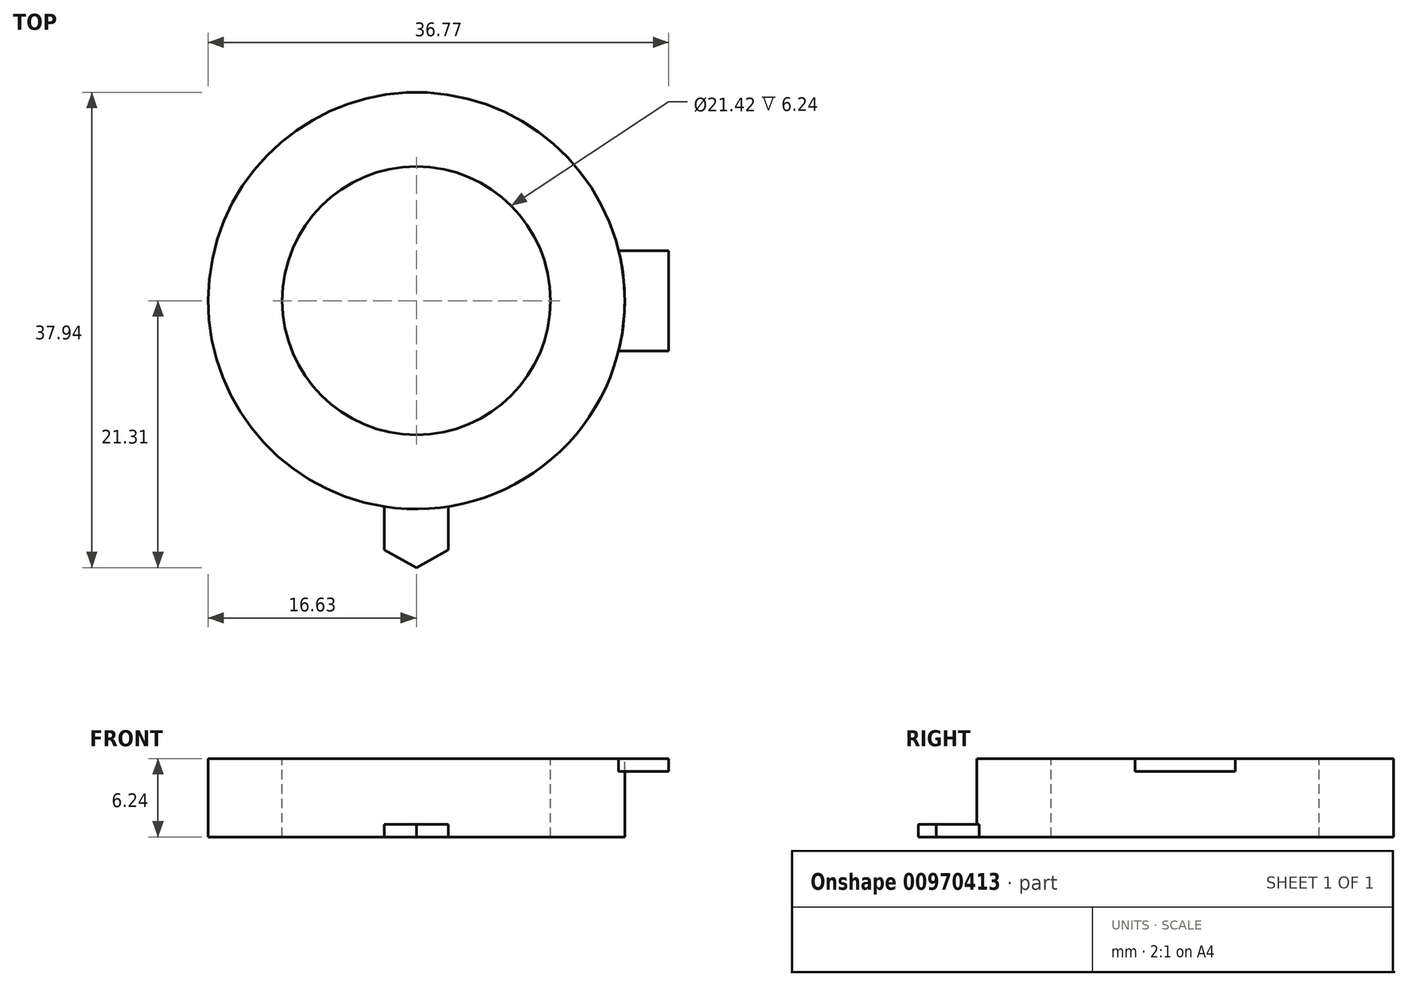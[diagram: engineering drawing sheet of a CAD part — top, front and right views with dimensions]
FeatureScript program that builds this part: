
annotation { "Feature Type Name" : "Feature", "Feature Type Description" : "" }
export const myFeature = defineFeature(function(context is Context, id is Id, definition is map)
    precondition{}
    {
        {
            var Q0;
            Q0=qCreatedBy(makeId("Top.planeOp"),FACE);
            var sketch = newSketch(context, id + "F0", { "sketchPlane" : qUnion([Q0])});
            skCircle(sketch, "E0", {"center": v(0, 0) * mm, "radius": 16.63 * mm});
            skLineSegment(sketch, "E1", {"start": v(0, 0) * mm, "end": v(0, -16.63) * mm, "construction": true});
            skLineSegment(sketch, "E2", {"start": v(-2.56, -16.43) * mm, "end": v(-2.56, -19.9) * mm});
            skLineSegment(sketch, "E3", {"start": v(-2.56, -19.9) * mm, "end": v(0, -21.31) * mm});
            skLineSegment(sketch, "E4", {"start": v(0, -21.3) * mm, "end": v(2.56, -19.9) * mm});
            skLineSegment(sketch, "E5", {"start": v(0, -21.31) * mm, "end": v(0, 16.63) * mm, "construction": true});
            skLineSegment(sketch, "E6", {"start": v(2.56, -19.9) * mm, "end": v(2.56, -16.43) * mm});
            skLineSegment(sketch, "E7", {"start": v(-2.56, -18.16) * mm, "end": v(0, -18.16) * mm, "construction": true});
            skLineSegment(sketch, "E8", {"start": v(0, -18.16) * mm, "end": v(2.56, -18.16) * mm, "construction": true});
            skSolve(sketch);
        }
        {
            var Q0;
            Q0=makeQuery(id+"F0.imprint","IMPRINT",FACE,{"disambiguationData":[TD([[makeQuery(id+"F0.imprint","IMPRINT",EDGE,{"derivedFrom":sQuery(id+"F0.wireOp",EDGE,"E0")}),1.0]])]});
            extrude(context, id + "F1", {"entities" : qUnion([Q0]), "depth" : 6.24 * mm, "offsetDistance" : 25 * mm});
        }
        {
            var Q0;
            {var subQ0=sQuery(id+"F0.wireOp",EDGE,"E2");Q0=makeQuery(id+"F0.imprint","IMPRINT",FACE,{"disambiguationData":[TD([[makeQuery(id+"F0.imprint","IMPRINT",EDGE,{"derivedFrom":subQ0}),1.0]])]});}
            extrude(context, id + "F2", {"entities" : qUnion([Q0]), "operationType" : NewBodyOperationType.ADD, "depth" : 1 * mm, "offsetDistance" : 25 * mm});
        }
        {
            var Q0;
            Q0=makeQuery(id+"F1.opExtrude","CAP_FACE",FACE,{"disambiguationData":[OSD([sQuery(id+"F0.wireOp",EDGE,"E0")])],"isStart":false});
            var sketch = newSketch(context, id + "F3", { "sketchPlane" : qUnion([Q0])});
            skCircle(sketch, "E9", {"center": v(0, 0) * mm, "radius": 10.71 * mm});
            skSolve(sketch);
        }
        {
            var Q0;
            Q0=makeQuery(id+"F3.imprint","IMPRINT",FACE,{"disambiguationData":[TD([[makeQuery(id+"F3.imprint","IMPRINT",EDGE,{"derivedFrom":sQuery(id+"F3.wireOp",EDGE,"E9")}),1.0]])]});
            extrude(context, id + "F4", {"entities" : qUnion([Q0]), "operationType" : NewBodyOperationType.REMOVE, "endBound" : BoundingType.THROUGH_ALL, "oppositeDirection" : true, "depth" : 25 * mm, "offsetDistance" : 25 * mm});
        }
        {
            var Q0;
            Q0=makeQuery(id+"F1.opExtrude","CAP_FACE",FACE,{"disambiguationData":[OSD([sQuery(id+"F0.wireOp",EDGE,"E0")])],"isStart":false});
            var sketch = newSketch(context, id + "F5", { "sketchPlane" : qUnion([Q0])});
            skLineSegment(sketch, "E10", {"start": v(16.14, 4) * mm, "end": v(20.14, 4) * mm});
            skLineSegment(sketch, "E11", {"start": v(20.14, 4) * mm, "end": v(20.14, -4) * mm});
            skLineSegment(sketch, "E12", {"start": v(20.14, -4) * mm, "end": v(16.14, -4) * mm});
            skLineSegment(sketch, "E13", {"start": v(18.14, 4) * mm, "end": v(18.14, 0) * mm, "construction": true});
            skLineSegment(sketch, "E14", {"start": v(18.14, -4) * mm, "end": v(18.14, 0) * mm, "construction": true});
            skPoint(sketch, "E15", {"position": v(18.14, 0) * mm});
            skCircle(sketch, "E16.0", {"center": v(0, 0) * mm, "radius": 16.63 * mm});
            skPoint(sketch, "E17", {"position": v(16.63, 0) * mm});
            skPoint(sketch, "E17.positionSnap0", {"position": v(20.14, 0) * mm});
            skArc(sketch, "E18", {"start": v(16.14, -4) * mm, "mid": v(16.63, 0) * mm, "end": v(16.14, 4) * mm});
            skSolve(sketch);
        }
        {
            var Q0;
            {var subQ0=sQuery(id+"F5.wireOp",EDGE,"E10");Q0=makeQuery(id+"F5.imprint","IMPRINT",FACE,{"disambiguationData":[TD([[makeQuery(id+"F5.imprint","IMPRINT",EDGE,{"derivedFrom":subQ0}),-1.0]])]});}
            extrude(context, id + "F6", {"entities" : qUnion([Q0]), "oppositeDirection" : true, "depth" : 1 * mm, "offsetDistance" : 25 * mm});
        }
    });
